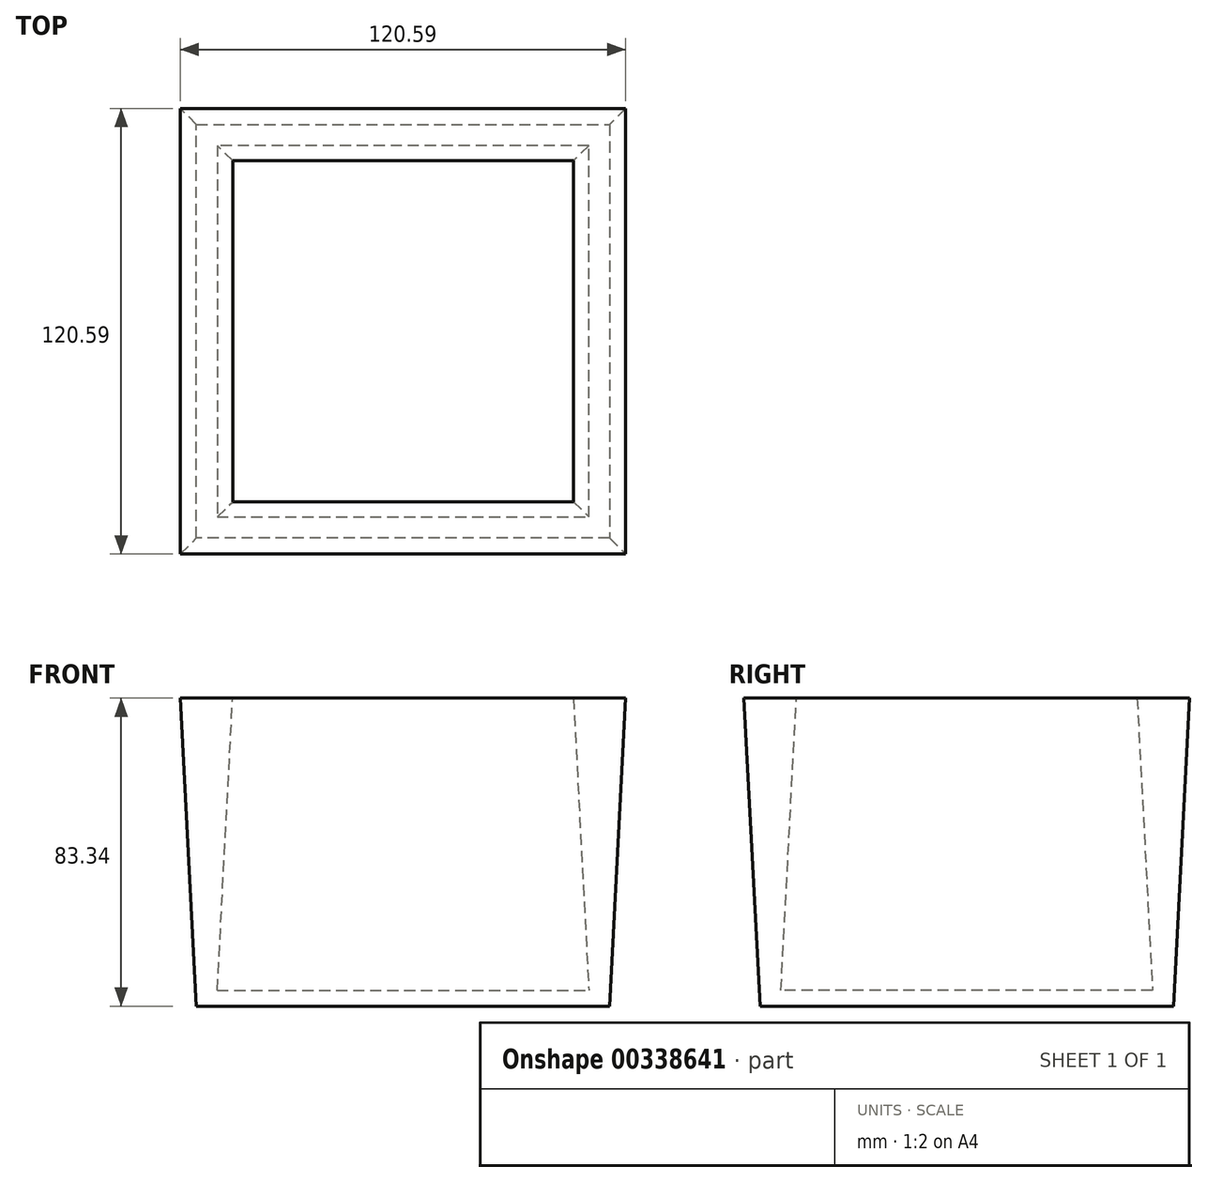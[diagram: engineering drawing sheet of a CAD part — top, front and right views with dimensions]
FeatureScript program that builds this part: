
annotation { "Feature Type Name" : "Feature", "Feature Type Description" : "" }
export const myFeature = defineFeature(function(context is Context, id is Id, definition is map)
    precondition{}
    {
        {
            var Q0;
            Q0=qCreatedBy(makeId("Top.planeOp"),FACE);
            var sketch = newSketch(context, id + "F0", { "sketchPlane" : qUnion([Q0])});
            skPoint(sketch, "E0.middle", {"position": v(0, 0) * mm});
            skLineSegment(sketch, "E1.bottom", {"start": v(-55.9, 55.62) * mm, "end": v(55.95, 55.62) * mm});
            skLineSegment(sketch, "E1.top", {"start": v(-55.9, -56.23) * mm, "end": v(55.95, -56.23) * mm});
            skLineSegment(sketch, "E1.left", {"start": v(-55.9, 55.62) * mm, "end": v(-55.9, -56.23) * mm});
            skLineSegment(sketch, "E1.right", {"start": v(55.95, 55.62) * mm, "end": v(55.95, -56.23) * mm});
            skLineSegment(sketch, "E2.bottom", {"start": v(-50.47, -50.8) * mm, "end": v(50.53, -50.8) * mm});
            skLineSegment(sketch, "E2.top", {"start": v(-50.47, 50.2) * mm, "end": v(50.53, 50.2) * mm});
            skLineSegment(sketch, "E2.left", {"start": v(-50.47, -50.8) * mm, "end": v(-50.47, 50.2) * mm});
            skLineSegment(sketch, "E2.right", {"start": v(50.53, -50.8) * mm, "end": v(50.53, 50.2) * mm});
            skPoint(sketch, "E3.firstSnap0", {"position": v(-55.9, -0.3) * mm});
            skSolve(sketch);
        }
        {
            var Q0;
            Q0 = qSketchRegion(id + "F0", true);
            extrude(context, id + "F1", {"entities" : qUnion([Q0]), "depth" : 83.34 * mm, "hasDraft" : true, "draftAngle" : 3 * degree});
        }
        {
            var Q0;
            Q0=makeQuery(id+"F0.imprint","IMPRINT",FACE,{"disambiguationData":[TD([[makeQuery(id+"F0.imprint","IMPRINT",EDGE,{"derivedFrom":sQuery(id+"F0.wireOp",EDGE,"E2.bottom")}),1.0]])]});
            extrude(context, id + "F2", {"entities" : qUnion([Q0]), "operationType" : NewBodyOperationType.ADD, "depth" : 4.26 * mm});
        }
    });
